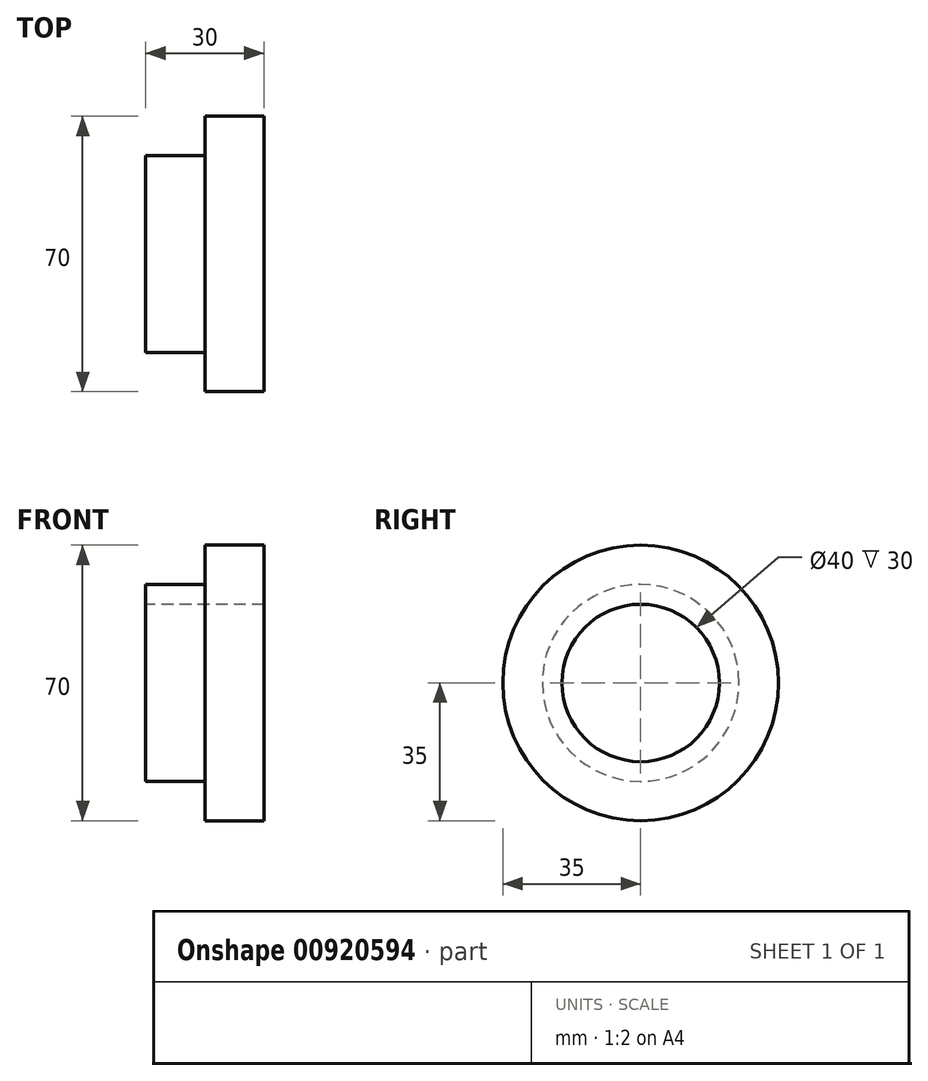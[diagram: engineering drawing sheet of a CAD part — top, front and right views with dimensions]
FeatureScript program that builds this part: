
annotation { "Feature Type Name" : "Feature", "Feature Type Description" : "" }
export const myFeature = defineFeature(function(context is Context, id is Id, definition is map)
    precondition{}
    {
        {
            var Q0;
            Q0=qCreatedBy(makeId("Front.planeOp"),FACE);
            var sketch = newSketch(context, id + "F0", { "sketchPlane" : qUnion([Q0])});
            skLineSegment(sketch, "E0", {"start": v(-8.13, 0) * mm, "end": v(8.13, 0) * mm, "construction": true});
            skLineSegment(sketch, "E1", {"start": v(0, 20) * mm, "end": v(30, 20) * mm});
            skLineSegment(sketch, "E2", {"start": v(30, 20) * mm, "end": v(30, 35) * mm});
            skLineSegment(sketch, "E3", {"start": v(30, 35) * mm, "end": v(15, 35) * mm});
            skLineSegment(sketch, "E4", {"start": v(15, 35) * mm, "end": v(15, 25) * mm});
            skLineSegment(sketch, "E5", {"start": v(15, 25) * mm, "end": v(0, 25) * mm});
            skLineSegment(sketch, "E6", {"start": v(0, 25) * mm, "end": v(0, 20) * mm});
            skSolve(sketch);
        }
        {
            var Q0;
            Q0=makeQuery(id+"F0.imprint","IMPRINT",FACE,{"disambiguationData":[TD([[makeQuery(id+"F0.imprint","IMPRINT",EDGE,{"derivedFrom":sQuery(id+"F0.wireOp",EDGE,"E1")}),1.0]])]});
            var Q1;
            Q1=sQuery(id+"F0.wireOp",EDGE,"E0");
            revolve(context, id + "F1", {"surfaceOperationType" : NewSurfaceOperationType.NEW, "entities" : qUnion([Q0]), "axis" : qUnion([Q1]), "revolveType" : RevolveType.FULL});
        }
    });
